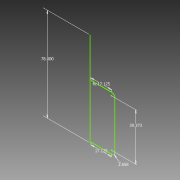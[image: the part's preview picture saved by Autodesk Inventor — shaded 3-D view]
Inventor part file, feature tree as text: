
AUTODESK INVENTOR PART (.ipt)
format: ipt  version: 2013 (Build 170138000, 138)  size: 67,072 bytes
history: native  units: in
note: dims shown in document units (in); Inventor stores cm internally (conversion verified against a paired STEP export)
features: sketch x1
ambient origin geometry x8: Origin, YZ Plane, XZ Plane, XY Plane, X Axis, Y Axis, Z Axis, Center Point
feature tree (1):
  sketch  "Sketch1"  dims[d0=78.0in d8=2.6575in d9=39.828in d10=17.125in d11=17.125in]
